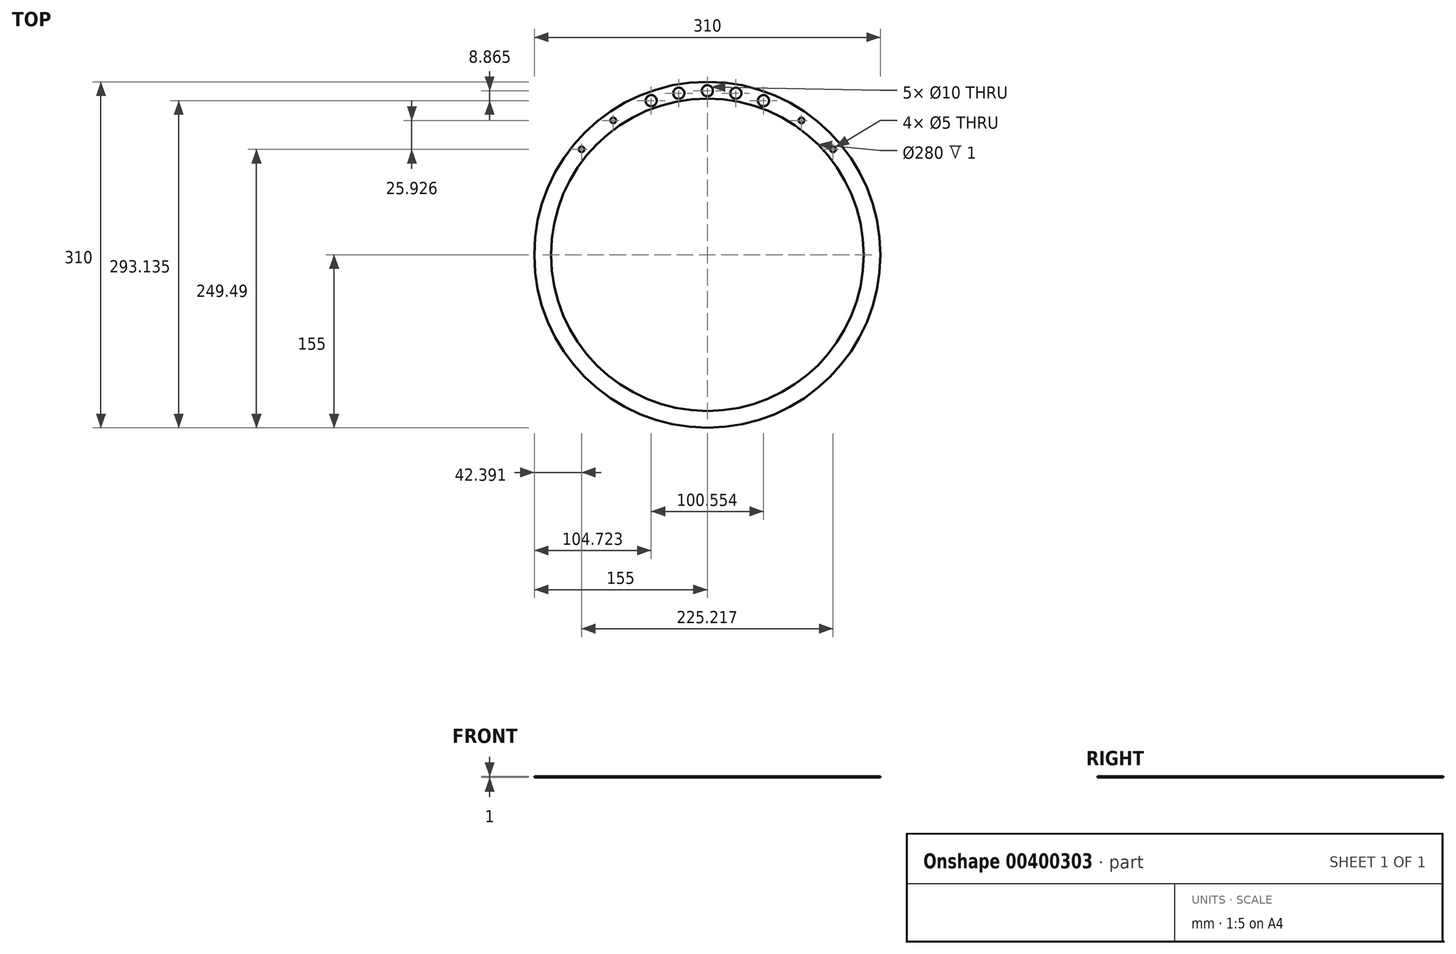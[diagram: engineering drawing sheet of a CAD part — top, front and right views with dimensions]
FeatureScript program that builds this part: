
annotation { "Feature Type Name" : "Feature", "Feature Type Description" : "" }
export const myFeature = defineFeature(function(context is Context, id is Id, definition is map)
    precondition{}
    {
        {
            var Q0;
            Q0=qCreatedBy(makeId("Top.planeOp"),FACE);
            var sketch = newSketch(context, id + "F0", { "sketchPlane" : qUnion([Q0])});
            skCircle(sketch, "E0", {"center": v(0, 0) * mm, "radius": 140 * mm});
            skCircle(sketch, "E1", {"center": v(0, 0) * mm, "radius": 155 * mm});
            skCircle(sketch, "E2", {"center": v(0, 147) * mm, "radius": 5 * mm});
            skLineSegment(sketch, "E3", {"start": v(0, 0) * mm, "end": v(0, 234.64) * mm, "construction": true});
            skCircle(sketch, "E4", {"center": v(0, 0) * mm, "radius": 147 * mm, "construction": true});
            skLineSegment(sketch, "E5", {"start": v(0, 0) * mm, "end": v(80.78, 221.95) * mm, "construction": true});
            skLineSegment(sketch, "E6", {"start": v(0, 0) * mm, "end": v(-80.78, 221.95) * mm, "construction": true});
            skLineSegment(sketch, "E7", {"start": v(0, 0) * mm, "end": v(-141.92, 202.68) * mm, "construction": true});
            skLineSegment(sketch, "E8", {"start": v(0, 0) * mm, "end": v(134.36, 191.88) * mm, "construction": true});
            skLineSegment(sketch, "E9", {"start": v(0, 0) * mm, "end": v(-185.19, 155.4) * mm, "construction": true});
            skLineSegment(sketch, "E10", {"start": v(0, 0) * mm, "end": v(178.66, 149.92) * mm, "construction": true});
            skLineSegment(sketch, "E11", {"start": v(0, 0) * mm, "end": v(0, -238) * mm, "construction": true});
            skCircle(sketch, "E12", {"center": v(-50.28, 138.13) * mm, "radius": 5 * mm});
            skCircle(sketch, "E13", {"center": v(50.28, 138.13) * mm, "radius": 5 * mm});
            skCircle(sketch, "E14", {"center": v(84.32, 120.42) * mm, "radius": 2.5 * mm});
            skCircle(sketch, "E15", {"center": v(112.6, 94.49) * mm, "radius": 2.5 * mm});
            skCircle(sketch, "E16", {"center": v(-84.32, 120.42) * mm, "radius": 2.5 * mm});
            skCircle(sketch, "E17", {"center": v(-112.6, 94.49) * mm, "radius": 2.5 * mm});
            skLineSegment(sketch, "E18", {"start": v(0, 0) * mm, "end": v(-40.15, 227.73) * mm, "construction": true});
            skLineSegment(sketch, "E19", {"start": v(0, 0) * mm, "end": v(40.49, 229.6) * mm, "construction": true});
            skCircle(sketch, "E20", {"center": v(-25.53, 144.77) * mm, "radius": 5 * mm});
            skCircle(sketch, "E21", {"center": v(25.53, 144.77) * mm, "radius": 5 * mm});
            skSolve(sketch);
        }
        {
            var Q0;
            Q0=makeQuery(id+"F0.imprint","IMPRINT",FACE,{"disambiguationData":[TD([[makeQuery(id+"F0.imprint","IMPRINT",EDGE,{"derivedFrom":sQuery(id+"F0.wireOp",EDGE,"E0")}),-1.0]])]});
            extrude(context, id + "F1", {"entities" : qUnion([Q0]), "depth" : 1 * mm});
        }
    });
